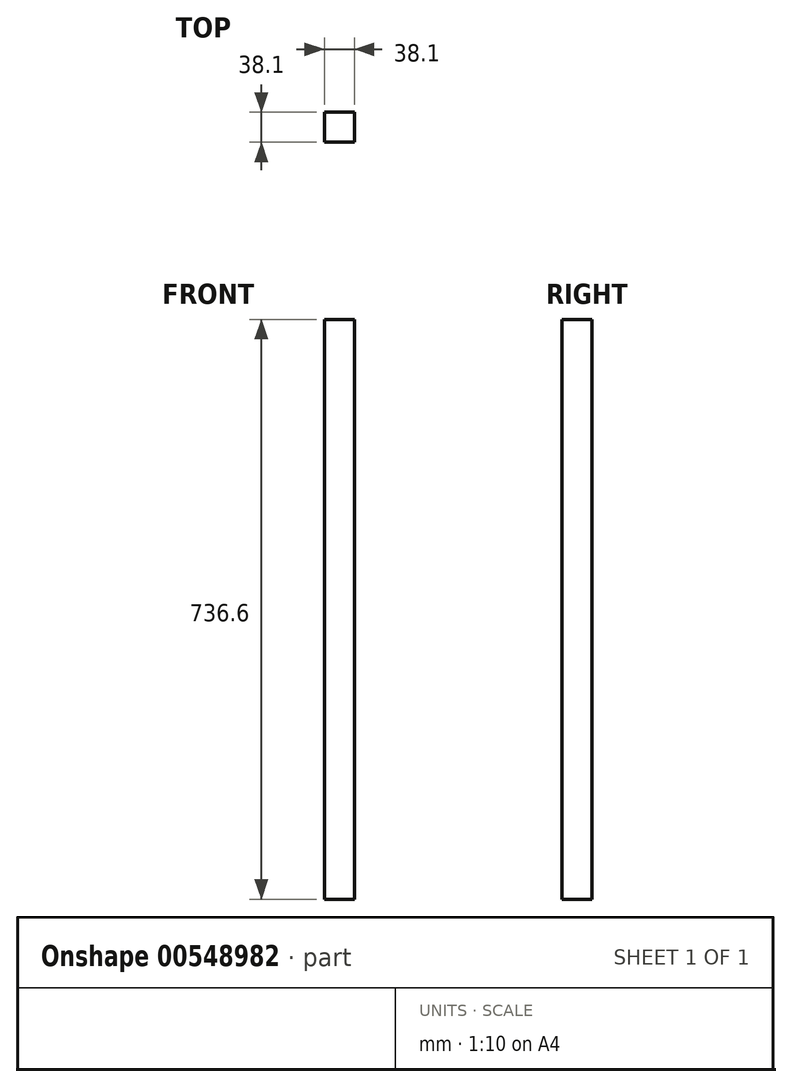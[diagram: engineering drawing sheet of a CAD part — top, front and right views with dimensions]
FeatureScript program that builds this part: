
annotation { "Feature Type Name" : "Feature", "Feature Type Description" : "" }
export const myFeature = defineFeature(function(context is Context, id is Id, definition is map)
    precondition{}
    {
        {
            var Q0;
            Q0=qCreatedBy(makeId("Top.planeOp"),FACE);
            var sketch = newSketch(context, id + "F0", { "sketchPlane" : qUnion([Q0])});
            skLineSegment(sketch, "E0.bottom", {"start": v(19.05, 19.05) * mm, "end": v(-19.05, 19.05) * mm});
            skLineSegment(sketch, "E0.top", {"start": v(19.05, -19.05) * mm, "end": v(-19.05, -19.05) * mm});
            skLineSegment(sketch, "E0.left", {"start": v(19.05, 19.05) * mm, "end": v(19.05, -19.05) * mm});
            skLineSegment(sketch, "E0.right", {"start": v(-19.05, 19.05) * mm, "end": v(-19.05, -19.05) * mm});
            skPoint(sketch, "E0.middle", {"position": v(0, 0) * mm});
            skSolve(sketch);
        }
        {
            var Q0;
            Q0=makeQuery(id+"F0.imprint","IMPRINT",FACE,{"disambiguationData":[TD([[makeQuery(id+"F0.imprint","IMPRINT",EDGE,{"derivedFrom":sQuery(id+"F0.wireOp",EDGE,"E0.bottom")}),1.0]])]});
            extrude(context, id + "F1", {"entities" : qUnion([Q0]), "depth" : 736.6 * mm, "offsetDistance" : 25.4 * mm});
        }
    });
